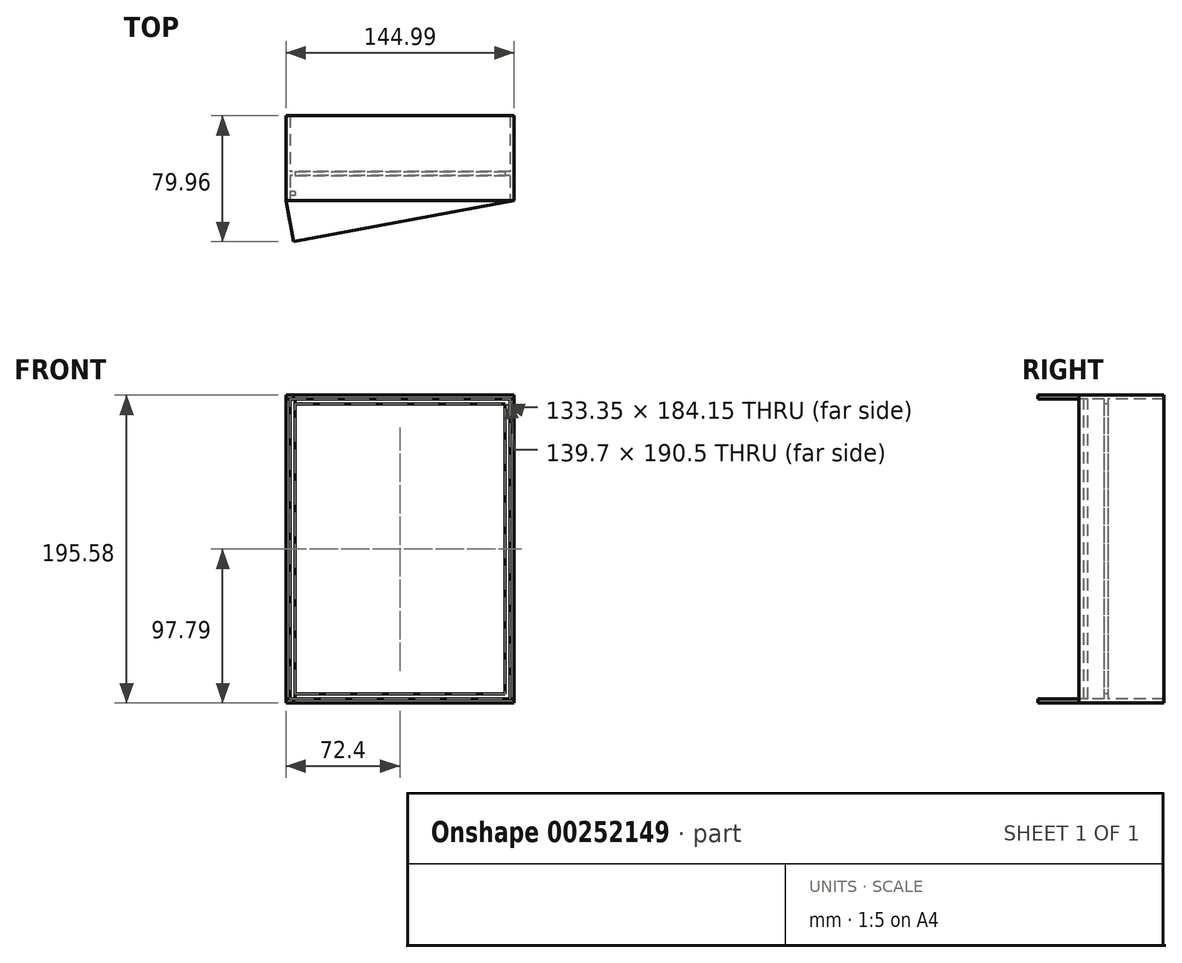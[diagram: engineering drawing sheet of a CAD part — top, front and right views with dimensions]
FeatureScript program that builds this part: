
annotation { "Feature Type Name" : "Feature", "Feature Type Description" : "" }
export const myFeature = defineFeature(function(context is Context, id is Id, definition is map)
    precondition{}
    {
        {
            var Q0;
            Q0=qCreatedBy(makeId("Front.planeOp"),FACE);
            var sketch = newSketch(context, id + "F0", { "sketchPlane" : qUnion([Q0])});
            skLineSegment(sketch, "E0.bottom", {"start": v(-69.85, 95.25) * mm, "end": v(69.85, 95.25) * mm});
            skLineSegment(sketch, "E0.top", {"start": v(-69.85, -95.25) * mm, "end": v(69.85, -95.25) * mm});
            skLineSegment(sketch, "E0.left", {"start": v(-69.85, 95.25) * mm, "end": v(-69.85, -95.25) * mm});
            skLineSegment(sketch, "E0.right", {"start": v(69.85, 95.25) * mm, "end": v(69.85, -95.25) * mm});
            skPoint(sketch, "E0.middle", {"position": v(0, 0) * mm});
            skSolve(sketch);
        }
        {
            var Q0;
            Q0=makeQuery(id+"F0.imprint","IMPRINT",FACE,{"disambiguationData":[TD([[makeQuery(id+"F0.imprint","IMPRINT",EDGE,{"derivedFrom":sQuery(id+"F0.wireOp",EDGE,"E0.bottom")}),-1.0]])]});
            extrude(context, id + "F1", {"entities" : qUnion([Q0]), "oppositeDirection" : true, "depth" : 53.97 * mm});
        }
        {
            var Q0;
            Q0=makeQuery(id+"F1.opExtrude","CAP_FACE",FACE,{"disambiguationData":[OSD([sQuery(id+"F0.wireOp",EDGE,"E0.bottom"),sQuery(id+"F0.wireOp",EDGE,"E0.top"),sQuery(id+"F0.wireOp",EDGE,"E0.left"),sQuery(id+"F0.wireOp",EDGE,"E0.right")])],"isStart":true});
            var Q1;
            Q1=makeQuery(id+"F1.opExtrude","CAP_FACE",FACE,{"disambiguationData":[OSD([sQuery(id+"F0.wireOp",EDGE,"E0.bottom"),sQuery(id+"F0.wireOp",EDGE,"E0.top"),sQuery(id+"F0.wireOp",EDGE,"E0.left"),sQuery(id+"F0.wireOp",EDGE,"E0.right")])],"isStart":false});
            shell(context, id + "F2", {"entities" : qUnion([Q0, Q1]), "thickness" : 2.54 * mm, "oppositeDirection" : true});
        }
        {
            var Q0;
            Q0=makeQuery(id+"F2.opShell","OFFSET_FACE",FACE,{"disambiguationData":[OSD([sQuery(id+"F0.wireOp",EDGE,"E0.left")])]});
            var sketch = newSketch(context, id + "F3", { "sketchPlane" : qUnion([Q0])});
            skLineSegment(sketch, "E1.bottom", {"start": v(3.18, -95.25) * mm, "end": v(5.72, -95.25) * mm});
            skLineSegment(sketch, "E1.top", {"start": v(3.17, 95.25) * mm, "end": v(5.71, 95.25) * mm});
            skLineSegment(sketch, "E1.left", {"start": v(3.18, -95.25) * mm, "end": v(3.17, 95.25) * mm});
            skLineSegment(sketch, "E1.right", {"start": v(5.72, -95.25) * mm, "end": v(5.71, 95.25) * mm});
            skSolve(sketch);
        }
        {
            var Q0;
            Q0=makeQuery(id+"F3.imprint","IMPRINT",FACE,{"disambiguationData":[TD([[makeQuery(id+"F3.imprint","IMPRINT",EDGE,{"derivedFrom":sQuery(id+"F3.wireOp",EDGE,"E1.bottom")}),-1.0]])]});
            extrude(context, id + "F4", {"entities" : qUnion([Q0]), "depth" : 3.17 * mm});
        }
        {
            var Q0;
            Q0=makeQuery(id+"F2.opShell","OFFSET_FACE",FACE,{"disambiguationData":[OSD([sQuery(id+"F0.wireOp",EDGE,"E0.left")])]});
            var sketch = newSketch(context, id + "F5", { "sketchPlane" : qUnion([Q0])});
            skLineSegment(sketch, "E2.bottom", {"start": v(18.42, -95.25) * mm, "end": v(15.88, -95.25) * mm});
            skLineSegment(sketch, "E2.top", {"start": v(18.41, 95.25) * mm, "end": v(15.87, 95.25) * mm});
            skLineSegment(sketch, "E2.left", {"start": v(18.42, -95.25) * mm, "end": v(18.41, 95.25) * mm});
            skLineSegment(sketch, "E2.right", {"start": v(15.88, -95.25) * mm, "end": v(15.87, 95.25) * mm});
            skSolve(sketch);
        }
        {
            var Q0;
            Q0=makeQuery(id+"F5.imprint","IMPRINT",FACE,{"disambiguationData":[TD([[makeQuery(id+"F5.imprint","IMPRINT",EDGE,{"derivedFrom":sQuery(id+"F5.wireOp",EDGE,"E2.bottom")}),-1.0]])]});
            extrude(context, id + "F6", {"entities" : qUnion([Q0]), "operationType" : NewBodyOperationType.ADD, "endBound" : BoundingType.UP_TO_NEXT, "depth" : 25.4 * mm});
        }
        {
            var Q0;
            Q0=qCreatedBy(makeId("Front.planeOp"),FACE);
            var sketch = newSketch(context, id + "F7", { "sketchPlane" : qUnion([Q0])});
            skLineSegment(sketch, "E3.bottom", {"start": v(-66.67, 92.08) * mm, "end": v(66.68, 92.08) * mm});
            skLineSegment(sketch, "E3.top", {"start": v(-66.68, -92.07) * mm, "end": v(66.68, -92.07) * mm});
            skLineSegment(sketch, "E3.left", {"start": v(-66.67, 92.08) * mm, "end": v(-66.68, -92.07) * mm});
            skLineSegment(sketch, "E3.right", {"start": v(66.68, 92.08) * mm, "end": v(66.68, -92.07) * mm});
            skPoint(sketch, "E3.middle", {"position": v(0, 0) * mm});
            skSolve(sketch);
        }
        {
            var Q0;
            Q0=makeQuery(id+"F7.imprint","IMPRINT",FACE,{"disambiguationData":[TD([[makeQuery(id+"F7.imprint","IMPRINT",EDGE,{"derivedFrom":sQuery(id+"F7.wireOp",EDGE,"E3.bottom")}),-1.0]])]});
            extrude(context, id + "F8", {"entities" : qUnion([Q0]), "operationType" : NewBodyOperationType.REMOVE, "oppositeDirection" : true, "depth" : 76.2 * mm});
        }
        {
            var Q0;
            Q0=makeQuery(id+"F1.opExtrude","SWEPT_FACE",FACE,{"disambiguationData":[OSD([sQuery(id+"F0.wireOp",EDGE,"E0.top")])]});
            var sketch = newSketch(context, id + "F9", { "sketchPlane" : qUnion([Q0])});
            skSolve(sketch);
        }
        {
            var Q0;
            {var subQ0=sQuery(id+"F0.wireOp",EDGE,"E0.top");Q0=makeQuery(id+"F9.imprint","IMPRINT",FACE,{"disambiguationData":[TD([[makeQuery(id+"F9.imprint","IMPRINT",EDGE,{"derivedFrom":makeQuery(id+"F1.opExtrude","CAP_EDGE",EDGE,{"disambiguationData":[OSD([subQ0])],"isStart":true})}),-1.0]])]});}
            var sketch = newSketch(context, id + "F10", { "sketchPlane" : qUnion([Q0])});
            skLineSegment(sketch, "E4", {"start": v(72.6, 0) * mm, "end": v(-67.58, 25.98) * mm});
            skLineSegment(sketch, "E5", {"start": v(-67.58, 25.98) * mm, "end": v(-72.4, 0) * mm});
            skLineSegment(sketch, "E6", {"start": v(-72.4, 0) * mm, "end": v(72.6, 0) * mm});
            skSolve(sketch);
        }
        {
            var Q0;
            {var subQ5=sQuery(id+"F10.wireOp",EDGE,"E4");Q0=makeQuery(id+"F10.imprint","IMPRINT",FACE,{"disambiguationData":[TD([[makeQuery(id+"F10.imprint","IMPRINT",EDGE,{"derivedFrom":subQ5}),1.0]])]});}
            extrude(context, id + "F11", {"entities" : qUnion([Q0]), "oppositeDirection" : true, "depth" : 2.54 * mm});
        }
        {
            var Q0;
            Q0=makeQuery(id+"F1.opExtrude","SWEPT_FACE",FACE,{"disambiguationData":[OSD([sQuery(id+"F0.wireOp",EDGE,"E0.bottom")])]});
            var sketch = newSketch(context, id + "F12", { "sketchPlane" : qUnion([Q0])});
            skLineSegment(sketch, "E7", {"start": v(72.4, 0) * mm, "end": v(-72.39, 0) * mm});
            skLineSegment(sketch, "E8", {"start": v(-72.39, 0) * mm, "end": v(-67.6, -25.95) * mm});
            skLineSegment(sketch, "E9", {"start": v(-67.6, -25.95) * mm, "end": v(72.4, 0) * mm});
            skSolve(sketch);
        }
        {
            var Q0;
            Q0=makeQuery(id+"F12.imprint","IMPRINT",FACE,{"disambiguationData":[TD([[makeQuery(id+"F12.imprint","IMPRINT",EDGE,{"derivedFrom":sQuery(id+"F12.wireOp",EDGE,"E7")}),-1.0]])]});
            extrude(context, id + "F13", {"entities" : qUnion([Q0]), "oppositeDirection" : true, "depth" : 2.54 * mm});
        }
    });
